# Revit family: Furniture Ekeby Bench - Cast In Place
name_source: partatom
category: Furniture
units: mm (PartAtom-declared; Revit-internal decimal feet)

## family parameters
Always vertical = Yes
Cut with Voids When Loaded = No
OmniClass Number = 23.21.23.13.15
Room Calculation Point = No
Shared = No
Work Plane-Based = No

## types (7) — shared parameters
BIMobject category = Bench & Park Bench
Description = Sofa Sofiero Detached
Edition number = 1
IFC Classification = Furniture
Manufacturer = Hags
Manufacturer name = HAGS
OmniClass Code = 23-21 23 13 15
OmniClass Description = Residential Sofas
Product Guid = 90e49432-c870-4a59-897e-b15016e8f9bd
Product SKU = Bench_Ekeby_Detached
Product data url = https://bimobject.com
Product url = https://hags.se
QR code = https://www.hags.com
URL = https://www.hags.com
Uniclass 1.4 Code = L8211
Uniclass 1.4 Description = Furniture
zero-valued in all types: Default Elevation

## per-type parameters (varying)
| type | Body material | Body material_90 | Construction material | Model | Product name |
| 8037101 Bark Brown / Black | Hags - Wood - Bark brown | Hags - Wood - Bark brown 90 | Hags - Steel - Powder coated - Black | 8037012 | Ekeby Park Bench |
| 8037103 Bark Brown/ Galvanized | Hags - Wood - Bark brown | Hags - Wood - Bark brown 90 | Hags - Steel - Galvanized | 8037014 | Ekeby Bench |
| 8037105 Green / Black | Hags - Steel - Powder coated - Green | Hags - Steel - Powder coated - Green | Hags - Steel - Powder coated - Black | 8037015 | Park Bench Ekeby |
| 8054888 Bilinga / Galvanised | Hags - Bilinga | Hags - Bilinga | Hags - Steel - Galvanized | 8037012 | Ekeby Park Bench |
| 8064356 Recycled Plastic / Galvanised | Hags - Recycled Plastic | Hags - Recycled Plastic | Hags - Steel - Galvanized | 8037012 | Ekeby Park Bench |
| 8064389 Recycled Plastic / Black | Hags - Recycled Plastic | Hags - Recycled Plastic | Hags - Steel - Powder coated - Black | 8037012 | Ekeby Park Bench |
| 8058460 Bilinga / Black | Hags - Bilinga | Hags - Bilinga | Hags - Steel - Powder coated - Black | 8037012 | Ekeby Park Bench |

## geometry (parser evidence)
native form markers: Sweep x3
no freeform markers — native parametric forms only
